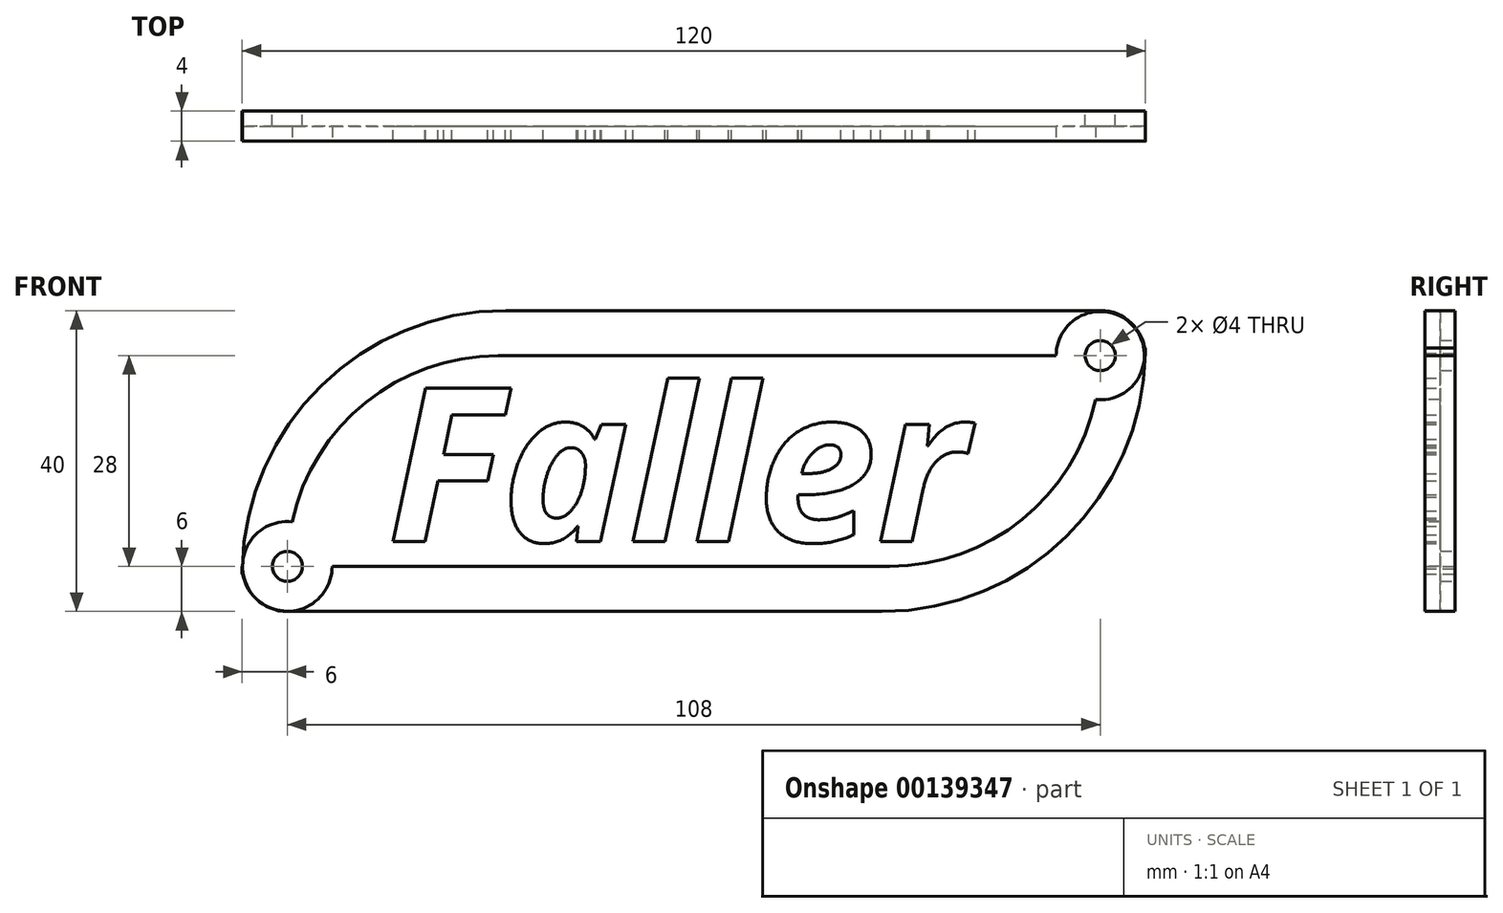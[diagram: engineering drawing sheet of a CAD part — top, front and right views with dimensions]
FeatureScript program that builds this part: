
annotation { "Feature Type Name" : "Feature", "Feature Type Description" : "" }
export const myFeature = defineFeature(function(context is Context, id is Id, definition is map)
    precondition{}
    {
        {
            var Q0;
            Q0=qCreatedBy(makeId("Front.planeOp"),FACE);
            var sketch = newSketch(context, id + "F0", { "sketchPlane" : qUnion([Q0])});
            skLineSegment(sketch, "E0.bottom", {"start": v(6, 0) * mm, "end": v(85, 0) * mm});
            skLineSegment(sketch, "E0.top", {"start": v(35, 40) * mm, "end": v(114, 40) * mm});
            skLineSegment(sketch, "E0.left", {"start": v(0, 5) * mm, "end": v(0, 6) * mm});
            skLineSegment(sketch, "E0.right", {"start": v(120, 34) * mm, "end": v(120, 35) * mm});
            skLineSegment(sketch, "E1", {"start": v(114, 0) * mm, "end": v(114, 40) * mm, "construction": true});
            skLineSegment(sketch, "E2", {"start": v(6, 0) * mm, "end": v(6, 40) * mm, "construction": true});
            skLineSegment(sketch, "E3", {"start": v(120, 6) * mm, "end": v(0, 6) * mm, "construction": true});
            skLineSegment(sketch, "E4", {"start": v(120, 34) * mm, "end": v(0, 34) * mm, "construction": true});
            skPoint(sketch, "E5.visualSharp", {"position": v(120, 40) * mm});
            skArc(sketch, "E5.filletArc", {"start": v(120, 34) * mm, "mid": v(118.24, 38.24) * mm, "end": v(114, 40) * mm});
            skPoint(sketch, "E6.visualSharp", {"position": v(0, 0) * mm});
            skArc(sketch, "E6.filletArc", {"start": v(0, 6) * mm, "mid": v(1.76, 1.76) * mm, "end": v(6, 0) * mm});
            skPoint(sketch, "E7.visualSharp", {"position": v(120, 0) * mm});
            skArc(sketch, "E7.filletArc", {"start": v(85, 0) * mm, "mid": v(109.75, 10.25) * mm, "end": v(120, 35) * mm});
            skPoint(sketch, "E8.visualSharp", {"position": v(0, 40) * mm});
            skArc(sketch, "E8.filletArc", {"start": v(35, 40) * mm, "mid": v(10.25, 29.75) * mm, "end": v(0, 5) * mm});
            skCircle(sketch, "E9", {"center": v(6, 6) * mm, "radius": 2 * mm});
            skCircle(sketch, "E10", {"center": v(114, 34) * mm, "radius": 2 * mm});
            skSolve(sketch);
        }
        {
            var Q0;
            Q0 = qSketchRegion(id + "F0", true);
            extrude(context, id + "F1", {"entities" : qUnion([Q0]), "depth" : 4 * mm});
        }
        {
            var Q0;
            Q0=makeQuery(id+"F1.opExtrude","CAP_FACE",FACE,{"disambiguationData":[OSD([sQuery(id+"F0.wireOp",EDGE,"E0.bottom"),sQuery(id+"F0.wireOp",EDGE,"E0.top"),sQuery(id+"F0.wireOp",EDGE,"E5.filletArc"),sQuery(id+"F0.wireOp",EDGE,"E6.filletArc"),sQuery(id+"F0.wireOp",EDGE,"E7.filletArc"),sQuery(id+"F0.wireOp",EDGE,"E8.filletArc"),sQuery(id+"F0.wireOp",EDGE,"E9"),sQuery(id+"F0.wireOp",EDGE,"E10")])],"isStart":false});
            var sketch = newSketch(context, id + "F2", { "sketchPlane" : qUnion([Q0])});
            skCircle(sketch, "E11", {"center": v(6, 6) * mm, "radius": 5.96 * mm});
            skCircle(sketch, "E12", {"center": v(114, 34) * mm, "radius": 5.87 * mm});
            skSolve(sketch);
        }
        {
            var Q0;
            Q0 = qSketchRegion(id + "F2", true);
            extrude(context, id + "F3", {"entities" : qUnion([Q0]), "operationType" : NewBodyOperationType.REMOVE, "oppositeDirection" : true, "depth" : 2 * mm});
        }
        {
            var Q0;
            Q0=makeQuery(id+"F1.opExtrude","CAP_FACE",FACE,{"disambiguationData":[OSD([sQuery(id+"F0.wireOp",EDGE,"E0.bottom"),sQuery(id+"F0.wireOp",EDGE,"E0.top"),sQuery(id+"F0.wireOp",EDGE,"E5.filletArc"),sQuery(id+"F0.wireOp",EDGE,"E6.filletArc"),sQuery(id+"F0.wireOp",EDGE,"E7.filletArc"),sQuery(id+"F0.wireOp",EDGE,"E8.filletArc"),sQuery(id+"F0.wireOp",EDGE,"E9"),sQuery(id+"F0.wireOp",EDGE,"E10")])],"isStart":false});
            var sketch = newSketch(context, id + "F4", { "sketchPlane" : qUnion([Q0])});
            skLineSegment(sketch, "E13.bottom", {"start": v(6, 6) * mm, "end": v(86, 6) * mm});
            skLineSegment(sketch, "E13.top", {"start": v(34, 34) * mm, "end": v(114, 34) * mm});
            skLineSegment(sketch, "E13.left", {"start": v(6, 6) * mm, "end": v(6, 6) * mm});
            skLineSegment(sketch, "E13.right", {"start": v(114, 34) * mm, "end": v(114, 34) * mm});
            skPoint(sketch, "E14.visualSharp", {"position": v(6, 34) * mm});
            skArc(sketch, "E14.filletArc", {"start": v(34, 34) * mm, "mid": v(14.2, 25.8) * mm, "end": v(6, 6) * mm});
            skPoint(sketch, "E15.visualSharp", {"position": v(114, 6) * mm});
            skArc(sketch, "E15.filletArc", {"start": v(86, 6) * mm, "mid": v(105.8, 14.2) * mm, "end": v(114, 34) * mm});
            skSolve(sketch);
        }
        {
            var Q0;
            {var subQ0=sQuery(id+"F4.wireOp",EDGE,"E15.filletArc");var subQ1=sQuery(id+"F4.wireOp",EDGE,"E13.bottom");var subQ2=makeQuery(id+"F4.imprint","INTERSECT",VERTEX,{"derivedFrom":[subQ1,subQ0]});Q0=makeQuery(id+"F4.imprint","IMPRINT",FACE,{"disambiguationData":[TD([[makeQuery(id+"F4.imprint","IMPRINT",EDGE,{"disambiguationData":[TD([[subQ2,1.0]])],"derivedFrom":subQ1}),1.0]])]});}
            extrude(context, id + "F5", {"entities" : qUnion([Q0]), "operationType" : NewBodyOperationType.REMOVE, "oppositeDirection" : true, "depth" : 2 * mm});
        }
        {
            var Q0;
            {var subQ0=sQuery(id+"F2.wireOp",EDGE,"E12");var subQ1=sQuery(id+"F2.wireOp",EDGE,"E11");Q0=makeQuery(id+"F5.boolean.opBoolean","MERGE",FACE,{"derivedFrom":[makeQuery(id+"F3.boolean.opBoolean","COPY",FACE,{"derivedFrom":makeQuery(id+"F3.opExtrude","CAP_FACE",FACE,{"disambiguationData":[OSD([subQ1])],"isStart":false})}),makeQuery(id+"F3.boolean.opBoolean","COPY",FACE,{"derivedFrom":makeQuery(id+"F3.opExtrude","CAP_FACE",FACE,{"disambiguationData":[OSD([subQ0])],"isStart":false})}),makeQuery(id+"F5.opExtrude","CAP_FACE",FACE,{"disambiguationData":[OSD([subQ1,subQ0,sQuery(id+"F4.wireOp",EDGE,"E13.bottom"),sQuery(id+"F4.wireOp",EDGE,"E13.top"),sQuery(id+"F4.wireOp",EDGE,"E14.filletArc"),sQuery(id+"F4.wireOp",EDGE,"E15.filletArc")])],"isStart":false})]});}
            var sketch = newSketch(context, id + "F6", { "sketchPlane" : qUnion([Q0])});
            skText(sketch, "E16", { "text": "Faller", "fontName": "OpenSans-BoldItalic.ttf"});
            const initialGuessF6  = {"E16": [0.01932, 0.0093, 1, 0, 0.02055]};
            skSetInitialGuess(sketch, initialGuessF6);
            skSolve(sketch);
        }
        {
            var Q0;
            Q0 = qSketchRegion(id + "F6", true);
            extrude(context, id + "F7", {"entities" : qUnion([Q0]), "operationType" : NewBodyOperationType.ADD, "depth" : 2 * mm});
        }
    });
